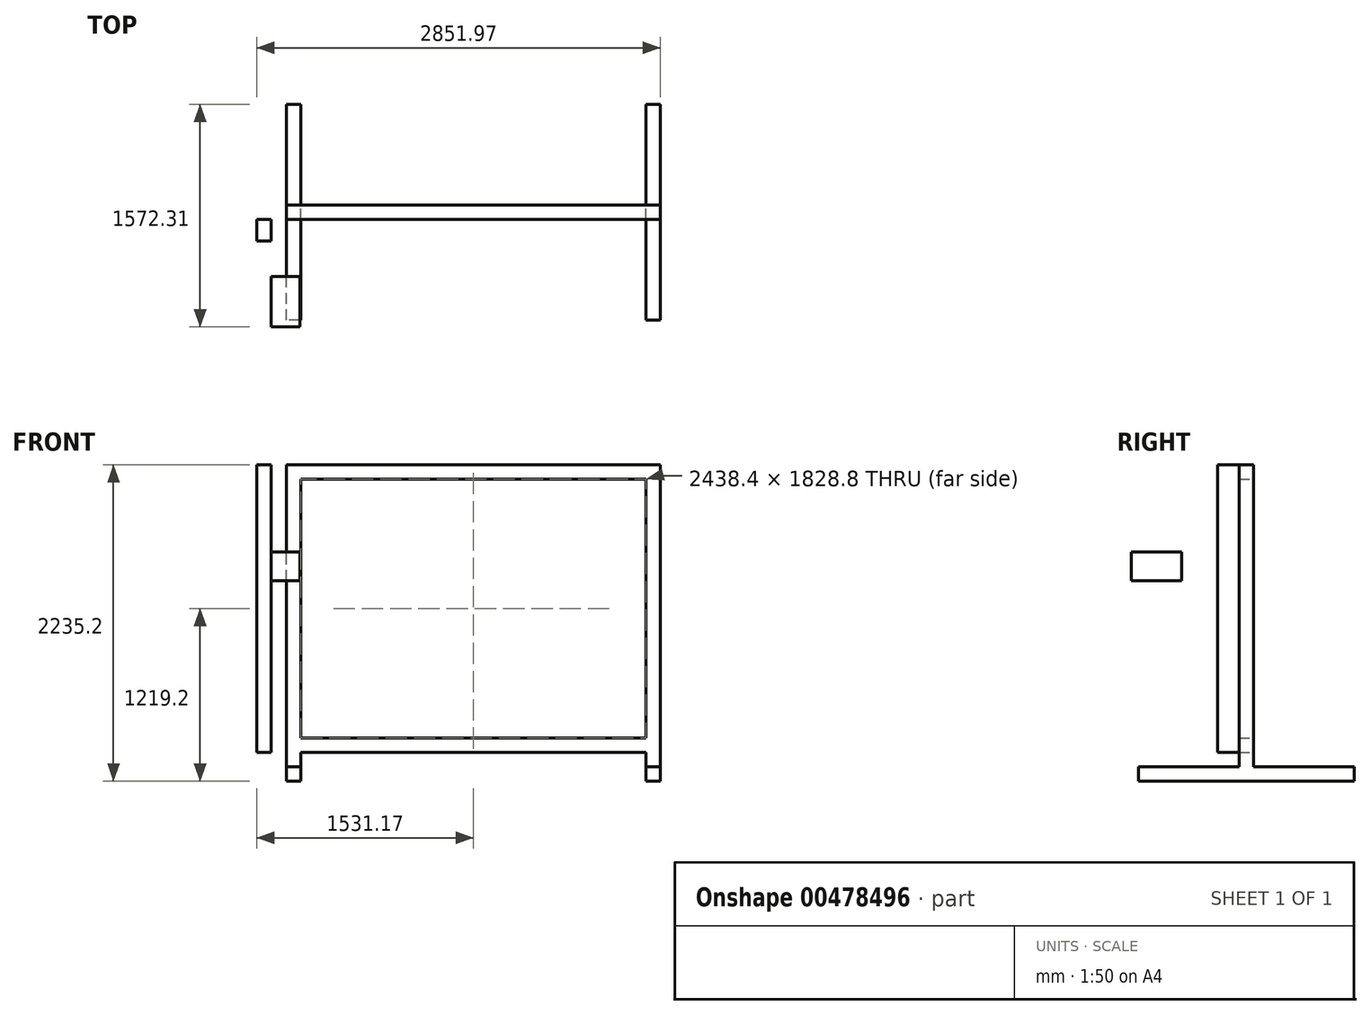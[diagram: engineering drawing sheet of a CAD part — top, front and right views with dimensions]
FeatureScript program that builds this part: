
annotation { "Feature Type Name" : "Feature", "Feature Type Description" : "" }
export const myFeature = defineFeature(function(context is Context, id is Id, definition is map)
    precondition{}
    {
        {
            var Q0;
            Q0=qCreatedBy(makeId("Front.planeOp"),FACE);
            var sketch = newSketch(context, id + "F0", { "sketchPlane" : qUnion([Q0])});
            skLineSegment(sketch, "E0", {"start": v(0, 203.2) * mm, "end": v(1219.2, 203.2) * mm});
            skLineSegment(sketch, "E1", {"start": v(1219.2, 203.2) * mm, "end": v(1219.2, 0) * mm});
            skLineSegment(sketch, "E2", {"start": v(1219.2, 0) * mm, "end": v(1320.8, 0) * mm});
            skLineSegment(sketch, "E3", {"start": v(1320.8, 0) * mm, "end": v(1320.8, 2235.2) * mm});
            skLineSegment(sketch, "E4", {"start": v(1320.8, 2235.2) * mm, "end": v(0, 2235.2) * mm});
            skLineSegment(sketch, "E5", {"start": v(0, 2133.6) * mm, "end": v(1219.2, 2133.6) * mm});
            skLineSegment(sketch, "E6", {"start": v(1219.2, 2133.6) * mm, "end": v(1219.2, 304.8) * mm});
            skLineSegment(sketch, "E7", {"start": v(1219.2, 304.8) * mm, "end": v(0, 304.8) * mm});
            skLineSegment(sketch, "E8", {"start": v(1219.2, 101.6) * mm, "end": v(1320.8, 101.6) * mm});
            skLineSegment(sketch, "E9.MirrorCS", {"start": v(-1219.2, 0) * mm, "end": v(-1320.8, 0) * mm});
            skLineSegment(sketch, "E10.MirrorCS", {"start": v(-1219.2, 203.2) * mm, "end": v(-1219.2, 0) * mm});
            skLineSegment(sketch, "E11.MirrorCS", {"start": v(-1219.2, 101.6) * mm, "end": v(-1320.8, 101.6) * mm});
            skLineSegment(sketch, "E12.MirrorCS", {"start": v(0, 203.2) * mm, "end": v(-1219.2, 203.2) * mm});
            skLineSegment(sketch, "E13.MirrorCS", {"start": v(-1219.2, 2133.6) * mm, "end": v(-1219.2, 304.8) * mm});
            skLineSegment(sketch, "E14.MirrorCS", {"start": v(-1320.8, 2235.2) * mm, "end": v(0, 2235.2) * mm});
            skLineSegment(sketch, "E15.MirrorCS", {"start": v(-1219.2, 304.8) * mm, "end": v(0, 304.8) * mm});
            skLineSegment(sketch, "E16.MirrorCS", {"start": v(-1320.8, 0) * mm, "end": v(-1320.8, 2235.2) * mm});
            skLineSegment(sketch, "E17.MirrorCS", {"start": v(0, 2133.6) * mm, "end": v(-1219.2, 2133.6) * mm});
            skSolve(sketch);
        }
        {
            var Q0;
            {var subQ2=sQuery(id+"F0.wireOp",EDGE,"E0");Q0=makeQuery(id+"F0.imprint","IMPRINT",FACE,{"disambiguationData":[TD([[makeQuery(id+"F0.imprint","IMPRINT",EDGE,{"derivedFrom":subQ2}),1.0]])]});}
            extrude(context, id + "F1", {"entities" : qUnion([Q0]), "depth" : 50.8 * mm, "hasSecondDirection" : true, "secondDirectionOppositeDirection" : true, "secondDirectionDepth" : 50.8 * mm});
        }
        {
            var Q0;
            {var subQ0=sQuery(id+"F0.wireOp",EDGE,"E9.MirrorCS");Q0=makeQuery(id+"F0.imprint","IMPRINT",FACE,{"disambiguationData":[TD([[makeQuery(id+"F0.imprint","IMPRINT",EDGE,{"derivedFrom":subQ0}),-1.0]])]});}
            var Q1;
            {var subQ0=sQuery(id+"F0.wireOp",EDGE,"E2");Q1=makeQuery(id+"F0.imprint","IMPRINT",FACE,{"disambiguationData":[TD([[makeQuery(id+"F0.imprint","IMPRINT",EDGE,{"derivedFrom":subQ0}),1.0]])]});}
            extrude(context, id + "F2", {"entities" : qUnion([Q0, Q1]), "operationType" : NewBodyOperationType.ADD, "depth" : 762 * mm, "hasSecondDirection" : true, "secondDirectionOppositeDirection" : true, "secondDirectionDepth" : 762 * mm});
        }
        {
            var Q0;
            Q0=makeQuery(id+"F1.opExtrude","CAP_FACE",FACE,{"disambiguationData":[OSD([sQuery(id+"F0.wireOp",EDGE,"E0"),sQuery(id+"F0.wireOp",EDGE,"E1"),sQuery(id+"F0.wireOp",EDGE,"E3"),sQuery(id+"F0.wireOp",EDGE,"E4"),sQuery(id+"F0.wireOp",EDGE,"E5"),sQuery(id+"F0.wireOp",EDGE,"E6"),sQuery(id+"F0.wireOp",EDGE,"E7"),sQuery(id+"F0.wireOp",EDGE,"E8"),sQuery(id+"F0.wireOp",EDGE,"E10.MirrorCS"),sQuery(id+"F0.wireOp",EDGE,"E11.MirrorCS"),sQuery(id+"F0.wireOp",EDGE,"E12.MirrorCS"),sQuery(id+"F0.wireOp",EDGE,"E13.MirrorCS"),sQuery(id+"F0.wireOp",EDGE,"E14.MirrorCS"),sQuery(id+"F0.wireOp",EDGE,"E15.MirrorCS"),sQuery(id+"F0.wireOp",EDGE,"E16.MirrorCS"),sQuery(id+"F0.wireOp",EDGE,"E17.MirrorCS")])],"isStart":false});
            var sketch = newSketch(context, id + "F3", { "sketchPlane" : qUnion([Q0])});
            skLineSegment(sketch, "E18.bottom", {"start": v(-1531.17, 2235.2) * mm, "end": v(-1429.57, 2235.2) * mm});
            skLineSegment(sketch, "E18.top", {"start": v(-1531.17, 203.2) * mm, "end": v(-1429.57, 203.2) * mm});
            skLineSegment(sketch, "E18.left", {"start": v(-1531.17, 2235.2) * mm, "end": v(-1531.17, 203.2) * mm});
            skLineSegment(sketch, "E18.right", {"start": v(-1429.57, 2235.2) * mm, "end": v(-1429.57, 203.2) * mm});
            skSolve(sketch);
        }
        {
            var Q0;
            Q0 = qSketchRegion(id + "F3", true);
            extrude(context, id + "F4", {"entities" : qUnion([Q0]), "operationType" : NewBodyOperationType.ADD, "depth" : 152.4 * mm});
        }
        {
            var Q0;
            Q0=makeQuery(id+"F4.opExtrude","SWEPT_FACE",FACE,{"disambiguationData":[OSD([sQuery(id+"F3.wireOp",EDGE,"E18.right")])]});
            var sketch = newSketch(context, id + "F5", { "sketchPlane" : qUnion([Q0])});
            skLineSegment(sketch, "E19.bottom", {"start": v(-810.31, 1619.17) * mm, "end": v(-454.71, 1619.17) * mm});
            skLineSegment(sketch, "E19.top", {"start": v(-810.31, 1415.97) * mm, "end": v(-454.71, 1415.97) * mm});
            skLineSegment(sketch, "E19.left", {"start": v(-810.31, 1619.17) * mm, "end": v(-810.31, 1415.97) * mm});
            skLineSegment(sketch, "E19.right", {"start": v(-454.71, 1619.17) * mm, "end": v(-454.71, 1415.97) * mm});
            skSolve(sketch);
        }
        {
            var Q0;
            Q0 = qSketchRegion(id + "F5", true);
            extrude(context, id + "F6", {"entities" : qUnion([Q0]), "operationType" : NewBodyOperationType.ADD, "depth" : 203.2 * mm});
        }
        {
            var Q0;
            Q0 = qSketchRegion(id + "F5", true);
            extrude(context, id + "F7", {"entities" : qUnion([Q0]), "operationType" : NewBodyOperationType.ADD, "depth" : 203.2 * mm});
        }
    });
